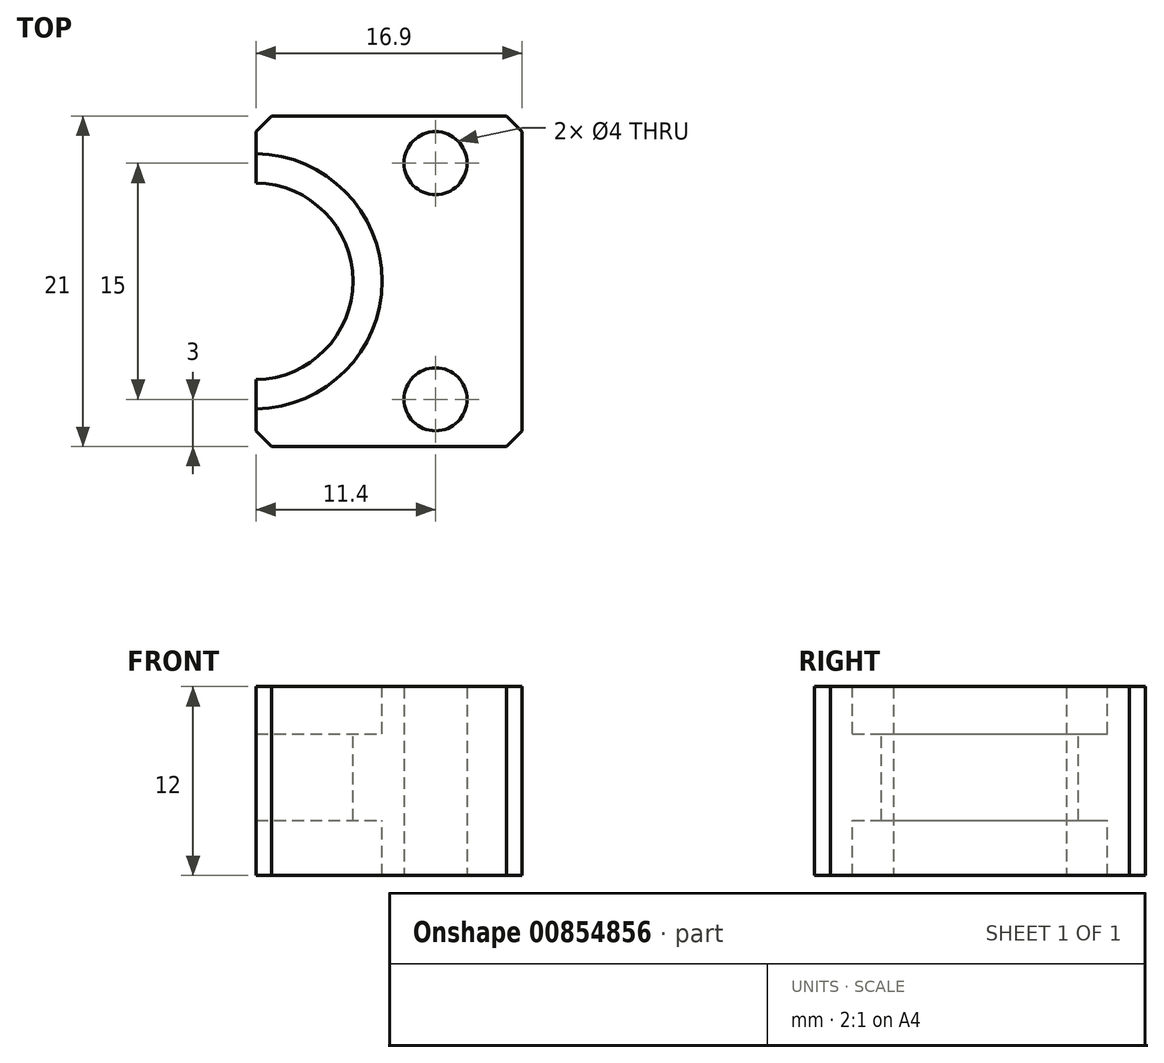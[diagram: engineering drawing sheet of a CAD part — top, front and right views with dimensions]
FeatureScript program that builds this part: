
annotation { "Feature Type Name" : "Feature", "Feature Type Description" : "" }
export const myFeature = defineFeature(function(context is Context, id is Id, definition is map)
    precondition{}
    {
        {
            var Q0;
            Q0=qCreatedBy(makeId("Top.planeOp"),FACE);
            var sketch = newSketch(context, id + "F0", { "sketchPlane" : qUnion([Q0])});
            skLineSegment(sketch, "E0.bottom", {"start": v(16, -10.5) * mm, "end": v(-0.9, -10.5) * mm});
            skLineSegment(sketch, "E0.top", {"start": v(16, 10.5) * mm, "end": v(-0.9, 10.5) * mm});
            skLineSegment(sketch, "E0.left", {"start": v(16, -10.5) * mm, "end": v(16, 10.5) * mm});
            skLineSegment(sketch, "E0.right", {"start": v(-16, -10.5) * mm, "end": v(-16, 10.5) * mm});
            skPoint(sketch, "E0.middle", {"position": v(0, 0) * mm});
            skCircle(sketch, "E1", {"center": v(-13, 7.5) * mm, "radius": 2 * mm});
            skCircle(sketch, "E2", {"center": v(-13, -7.5) * mm, "radius": 2 * mm});
            skCircle(sketch, "E3", {"center": v(10.5, 7.5) * mm, "radius": 2 * mm});
            skCircle(sketch, "E4", {"center": v(10.5, -7.5) * mm, "radius": 2 * mm});
            skLineSegment(sketch, "E5", {"start": v(16, 0) * mm, "end": v(-1, 0) * mm, "construction": true});
            skArc(sketch, "E6", {"start": v(-0.9, -1) * mm, "mid": v(0, 0) * mm, "end": v(-0.9, 1) * mm});
            skLineSegment(sketch, "E7.left", {"start": v(-1.1, -10.5) * mm, "end": v(-1.1, -1) * mm});
            skLineSegment(sketch, "E7.right", {"start": v(-0.9, -10.5) * mm, "end": v(-0.9, -1) * mm});
            skLineSegment(sketch, "E8.trimOffspring", {"start": v(-1.1, 10.5) * mm, "end": v(-16, 10.5) * mm});
            skLineSegment(sketch, "E9.trimOffspring", {"start": v(-1.1, -10.5) * mm, "end": v(-16, -10.5) * mm});
            skArc(sketch, "E10.trimOffspring", {"start": v(-1.1, 1) * mm, "mid": v(-2, 0) * mm, "end": v(-1.1, -1) * mm});
            skLineSegment(sketch, "E11.trimOffspring", {"start": v(-1.1, 1) * mm, "end": v(-1.1, 10.5) * mm});
            skLineSegment(sketch, "E12.trimOffspring", {"start": v(-0.9, 1) * mm, "end": v(-0.9, 10.5) * mm});
            skLineSegment(sketch, "E13", {"start": v(-16, 10.5) * mm, "end": v(-1.1, 10.5) * mm});
            skSolve(sketch);
        }
        {
            var Q0;
            Q0=makeQuery(id+"F0.imprint","IMPRINT",FACE,{"disambiguationData":[TD([[makeQuery(id+"F0.imprint","IMPRINT",EDGE,{"derivedFrom":sQuery(id+"F0.wireOp",EDGE,"E0.bottom")}),-1.0]])]});
            extrude(context, id + "F1", {"entities" : qUnion([Q0]), "depth" : 12 * mm, "offsetDistance" : 25 * mm});
        }
        {
            var Q0;
            Q0=makeQuery(id+"F1.opExtrude","CAP_FACE",FACE,{"disambiguationData":[OSD([sQuery(id+"F0.wireOp",EDGE,"E0.bottom"),sQuery(id+"F0.wireOp",EDGE,"E0.top"),sQuery(id+"F0.wireOp",EDGE,"E0.left"),sQuery(id+"F0.wireOp",EDGE,"E0.right"),sQuery(id+"F0.wireOp",EDGE,"E1"),sQuery(id+"F0.wireOp",EDGE,"E2"),sQuery(id+"F0.wireOp",EDGE,"E3"),sQuery(id+"F0.wireOp",EDGE,"E4"),sQuery(id+"F0.wireOp",EDGE,"E6")])],"isStart":false});
            var sketch = newSketch(context, id + "F2", { "sketchPlane" : qUnion([Q0])});
            skCircle(sketch, "E14", {"center": v(-1, 0) * mm, "radius": 8.1 * mm});
            skSolve(sketch);
        }
        {
            var Q0;
            Q0 = qSketchRegion(id + "F2", true);
            extrude(context, id + "F3", {"entities" : qUnion([Q0]), "operationType" : NewBodyOperationType.REMOVE, "oppositeDirection" : true, "depth" : 3 * mm, "offsetDistance" : 25 * mm});
        }
        {
            var Q0;
            Q0=makeQuery(id+"F3.boolean.opBoolean","COPY",FACE,{"derivedFrom":makeQuery(id+"F3.opExtrude","CAP_FACE",FACE,{"disambiguationData":[OSD([sQuery(id+"F2.wireOp",EDGE,"E14")])],"isStart":false})});
            var sketch = newSketch(context, id + "F4", { "sketchPlane" : qUnion([Q0])});
            skCircle(sketch, "E15", {"center": v(-1, 0) * mm, "radius": 6.25 * mm});
            skSolve(sketch);
        }
        {
            var Q0;
            Q0 = qSketchRegion(id + "F4", true);
            extrude(context, id + "F5", {"entities" : qUnion([Q0]), "operationType" : NewBodyOperationType.REMOVE, "oppositeDirection" : true, "depth" : 5.5 * mm, "offsetDistance" : 25 * mm});
        }
        {
            var Q0;
            Q0=makeQuery(id+"F5.boolean.opBoolean","COPY",FACE,{"derivedFrom":makeQuery(id+"F5.opExtrude","CAP_FACE",FACE,{"disambiguationData":[OSD([sQuery(id+"F4.wireOp",EDGE,"E15")])],"isStart":false})});
            var sketch = newSketch(context, id + "F6", { "sketchPlane" : qUnion([Q0])});
            skCircle(sketch, "E16", {"center": v(-1, 0) * mm, "radius": 8.1 * mm});
            skSolve(sketch);
        }
        {
            var Q0;
            Q0 = qSketchRegion(id + "F6", true);
            extrude(context, id + "F7", {"entities" : qUnion([Q0]), "operationType" : NewBodyOperationType.REMOVE, "oppositeDirection" : true, "depth" : 25 * mm, "offsetDistance" : 25 * mm});
        }
        {
            var Q0;
            Q0=makeQuery(id+"F1.opExtrude","SWEPT_EDGE",EDGE,{"disambiguationData":[OSD([sQuery(id+"F0.wireOp",EDGE,"E0.top"),sQuery(id+"F0.wireOp",EDGE,"E0.right")])]});
            var Q1;
            Q1=makeQuery(id+"F1.opExtrude","SWEPT_EDGE",EDGE,{"disambiguationData":[OSD([sQuery(id+"F0.wireOp",EDGE,"E0.top"),sQuery(id+"F0.wireOp",EDGE,"E0.left")])]});
            var Q2;
            Q2=makeQuery(id+"F1.opExtrude","SWEPT_EDGE",EDGE,{"disambiguationData":[OSD([sQuery(id+"F0.wireOp",EDGE,"E0.bottom"),sQuery(id+"F0.wireOp",EDGE,"E0.left")])]});
            var Q3;
            Q3=makeQuery(id+"F1.opExtrude","SWEPT_EDGE",EDGE,{"disambiguationData":[OSD([sQuery(id+"F0.wireOp",EDGE,"E0.bottom"),sQuery(id+"F0.wireOp",EDGE,"E0.right")])]});
            chamfer(context, id + "F8", {"entities" : qUnion([Q0, Q1, Q2, Q3]), "width" : 1 * mm, "tangentPropagation" : true});
        }
    });
